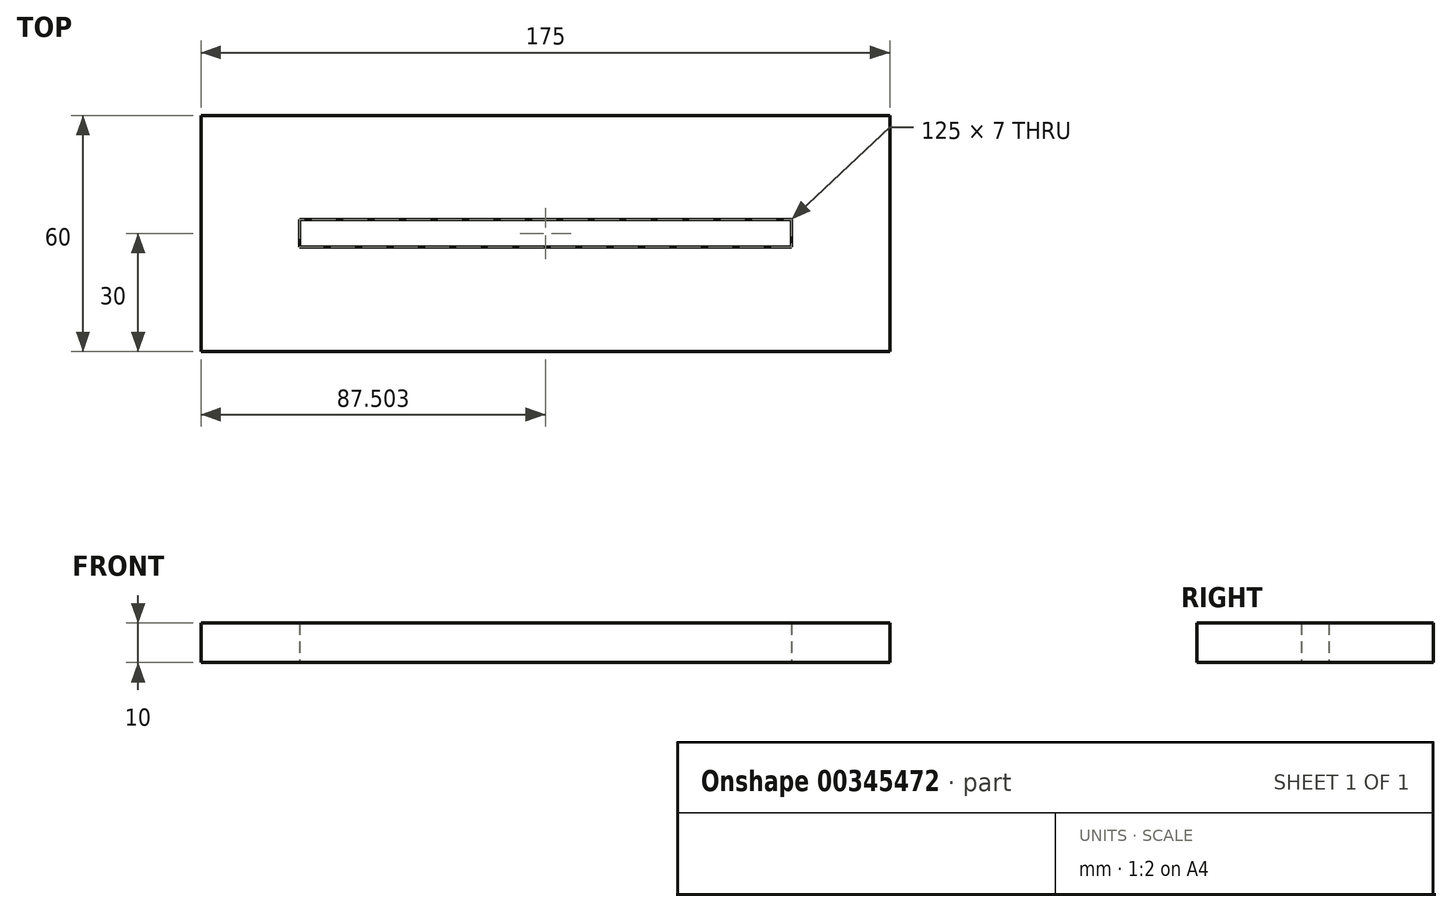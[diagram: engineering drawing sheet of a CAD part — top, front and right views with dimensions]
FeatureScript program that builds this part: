
annotation { "Feature Type Name" : "Feature", "Feature Type Description" : "" }
export const myFeature = defineFeature(function(context is Context, id is Id, definition is map)
    precondition{}
    {
        {
            var Q0;
            Q0=qCreatedBy(makeId("Top.planeOp"),FACE);
            var sketch = newSketch(context, id + "F0", { "sketchPlane" : qUnion([Q0])});
            skLineSegment(sketch, "E0.bottom", {"start": v(-44.07, 33.5) * mm, "end": v(130.93, 33.5) * mm});
            skLineSegment(sketch, "E0.top", {"start": v(-44.07, -26.5) * mm, "end": v(130.93, -26.5) * mm});
            skLineSegment(sketch, "E0.left", {"start": v(-44.07, 33.5) * mm, "end": v(-44.07, -26.5) * mm});
            skLineSegment(sketch, "E0.right", {"start": v(130.93, 33.5) * mm, "end": v(130.93, -26.5) * mm});
            skLineSegment(sketch, "E1.bottom", {"start": v(-19.07, 7) * mm, "end": v(105.93, 7) * mm});
            skLineSegment(sketch, "E1.top", {"start": v(-19.07, 0) * mm, "end": v(105.93, 0) * mm});
            skLineSegment(sketch, "E1.left", {"start": v(-19.07, 7) * mm, "end": v(-19.07, 0) * mm});
            skLineSegment(sketch, "E1.right", {"start": v(105.93, 7) * mm, "end": v(105.93, 0) * mm});
            skSolve(sketch);
        }
        {
            var Q0;
            Q0=makeQuery(id+"F0.imprint","IMPRINT",FACE,{"disambiguationData":[TD([[makeQuery(id+"F0.imprint","IMPRINT",EDGE,{"derivedFrom":sQuery(id+"F0.wireOp",EDGE,"E0.bottom")}),-1.0]])]});
            extrude(context, id + "F1", {"entities" : qUnion([Q0]), "depth" : 10 * mm});
        }
    });
